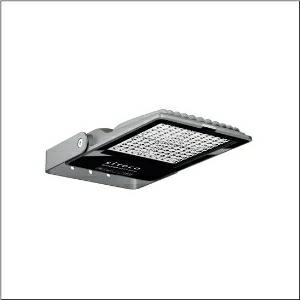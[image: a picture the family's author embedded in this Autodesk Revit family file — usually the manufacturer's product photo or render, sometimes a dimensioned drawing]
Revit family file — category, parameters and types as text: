
# Revit family: sicompact_31_mini___pl32_5xa7571f1k23_4e98
name_source: partatom
category: Lighting Fixtures
units: mm (PartAtom-declared; Revit-internal decimal feet)

## family parameters
Cut with Voids When Loaded = No
Host = Face
Light Source = No
Part Type = Normal
Room Calculation Point = No
Round Connector Dimension = Use Diameter
Shared = No

## types (1)
- SiCompact 31 mini  PL32 (1 x LED, 20000 lm, 130 W, 3000K)
    Apparent Load = 130 VA
    CIE Flux Codes = 32 69 98 100 100
    Color Rendering = 70
    Color Temperature = 3000K
    Default Elevation = 1800 mm
    Description = SiCompact 31 mini, floodlight, primary light control with lens, of plastic, of toughened safety glass, transparent, light distribution: PL32, light emission: direct distribution, primary light characteristic: asymmetric, installation type: surface-mounted, LED, High Power LED, rated luminous flux: 20.000lm, luminous efficacy: 154lm/W, light colour: 730, colour temperature: 3000K, control gear: ON/OFF, with cable, 3x 1.5mm², mains connection: 220..240V, AC, 50/60Hz, connection cable pre-assembled, cable length: 2m, rated input power: 130W, of diecast aluminium, specular, metallic grey (RAL 9006), length: 461mm, width: 261mm, height: 62mm, bracket, of sheet steel, coated, metallic grey (RAL 9006), ON/OFF, protection rating (complete): IP66, insulation class (complete): insulation class I (protective earthing), certification: CE, ENEC, impact resistance: IK08, permissible operating ambient temperature: -40..+45°C, packaging unit: 1 piece

Light Distribution: PL32
    Height = 62 mm  [stored 0.203412 ft]
    Lamp = 1 x LED
    Lamp Light Flux = 20000 lm
    Lamp Power = 130 W
    Lamp count = 1
    Length = 460 mm
    Luminous efficacy = 154 lm/W
    Manufacturer = Siteco
    ModVariant = No
    Model = 5XA7571F1K23
    Mounting Place = Wall
    Mounting Type = Surface mounted
    Number of Poles = 1
    OnlyDefault = Yes
    Power Factor = 1
    Product Name = SiCompact 31 mini | PL32
    Product group = floodlight | wall mounted
    ProductGroupID = 2002
    Protection Class = Protection class I
    Protection Degree = IP 66
    RLX_Detail_Level = 1
    RLX_Emergency_Light_Flux = 0 lm
    RLX_Emergency_Type = 0
    RLX_Emergency_Type_DB = No
    RlxData = <blob elided: 126161 chars, md5=b0311dc4>
    Socket = socket
    Standby Power = 0 W
    System Light Flux = 20000 lm
    System Power = 130 W
    Type Comments = Product without accessories
    Type Image = l_1006951.jpg
    URL = http://relux.com
    VarID = ---
    Voltage = 0 V
    Weight = 0.00 kg
    Width = 260 mm

note: [stored X ft] marks values corroborated as IEEE doubles in the binary element streams (Revit-internal decimal feet)

## geometry (parser evidence)
native form markers: Blend x4, Sweep x13
no freeform markers — native parametric forms only
